# Revit family: Bathtub-Aquatic-MONTROSE_II
name_source: partatom
category: Plumbing Fixtures
units: mm (PartAtom-declared; Revit-internal decimal feet)

## family parameters
Always vertical = Yes
Cut with Voids When Loaded = No
OmniClass Number = 23.45.05.14.21.17
OmniClass Title = Therapeutic Whirlpool Baths
Part Type = Normal
Room Calculation Point = No
Round Connector Dimension = Use Radius
Shared = No
Work Plane-Based = No

## types (1)
- 72" x 36" x 21 3/4"
    ADA = No
    Architectural Design Manual = http://www.aquaticbath.com
    Assembly Code = D2010710
    Default Elevation = 0' - 0"
    Depth = 3' - 0"
    Description = Acrylic Surface
    Drain = MONTROSE II Drain
    Drain Radius = 0' - 1"
    Finish = Acrylic-Aquatic-White
    Flow = 0.0 L/s
    Height = 1' - 9 3/4"
    Manufacturer = Aquatic
    MasterFormat Number = 22.41.19
    MasterFormat Title = Resitential Bathtubs
    Model = 4272621
    Revision Date = 5/1/2012
    Series = Hydrotherapy
    Supply Radius = 0' - 0 1/2"
    Tag = BATHTUB
    Type Comments = MONTROSE II
    URL = http://www.aquaticbath.com
    Water Supply = MONTROSE II Supply
    Whirlpool = Yes
    Width = 6' - 0"

## geometry (parser evidence)
native form markers: Sweep x4
no freeform markers — native parametric forms only
